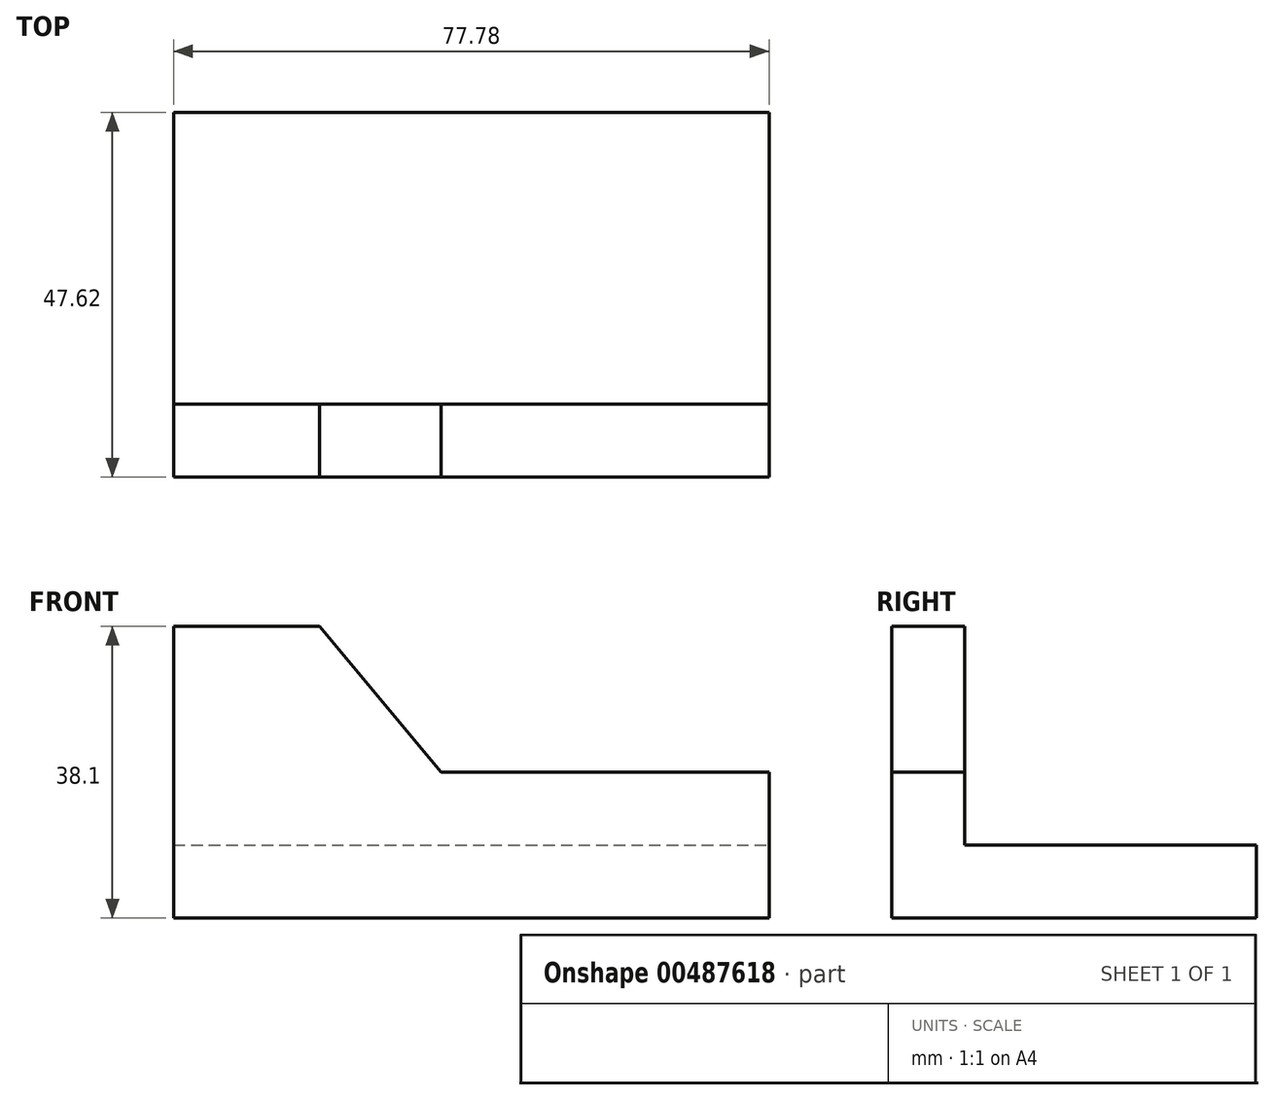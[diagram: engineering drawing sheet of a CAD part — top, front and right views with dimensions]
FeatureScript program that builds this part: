
annotation { "Feature Type Name" : "Feature", "Feature Type Description" : "" }
export const myFeature = defineFeature(function(context is Context, id is Id, definition is map)
    precondition{}
    {
        {
            var Q0;
            Q0=qCreatedBy(makeId("Top.planeOp"),FACE);
            var sketch = newSketch(context, id + "F0", { "sketchPlane" : qUnion([Q0])});
            skLineSegment(sketch, "E0.bottom", {"start": v(-38.9, 23.81) * mm, "end": v(38.9, 23.81) * mm});
            skLineSegment(sketch, "E0.top", {"start": v(-38.9, -23.81) * mm, "end": v(38.9, -23.81) * mm});
            skLineSegment(sketch, "E0.left", {"start": v(-38.9, 23.81) * mm, "end": v(-38.9, -23.81) * mm});
            skLineSegment(sketch, "E0.right", {"start": v(38.9, 23.81) * mm, "end": v(38.9, -23.81) * mm});
            skPoint(sketch, "E0.middle", {"position": v(0, 0) * mm});
            skSolve(sketch);
        }
        {
            var Q0;
            Q0 = qSketchRegion(id + "F0", true);
            extrude(context, id + "F1", {"entities" : qUnion([Q0]), "depth" : 9.52 * mm});
        }
        {
            var Q0;
            Q0=makeQuery(id+"F1.opExtrude","SWEPT_FACE",FACE,{"disambiguationData":[OSD([sQuery(id+"F0.wireOp",EDGE,"E0.top")])]});
            var sketch = newSketch(context, id + "F2", { "sketchPlane" : qUnion([Q0])});
            skLineSegment(sketch, "E1", {"start": v(-38.9, 0) * mm, "end": v(-38.9, 38.1) * mm});
            skLineSegment(sketch, "E2", {"start": v(-38.9, 38.1) * mm, "end": v(-19.84, 38.1) * mm});
            skLineSegment(sketch, "E3", {"start": v(-19.84, 38.1) * mm, "end": v(-3.97, 19.05) * mm});
            skLineSegment(sketch, "E4", {"start": v(-3.97, 19.05) * mm, "end": v(38.9, 19.05) * mm});
            skLineSegment(sketch, "E5", {"start": v(38.9, 19.05) * mm, "end": v(38.9, 0) * mm});
            skLineSegment(sketch, "E6", {"start": v(38.9, 0) * mm, "end": v(-38.9, 0) * mm});
            skSolve(sketch);
        }
        {
            var Q0;
            Q0 = qSketchRegion(id + "F2", true);
            extrude(context, id + "F3", {"entities" : qUnion([Q0]), "operationType" : NewBodyOperationType.ADD, "oppositeDirection" : true, "depth" : 9.52 * mm});
        }
    });
